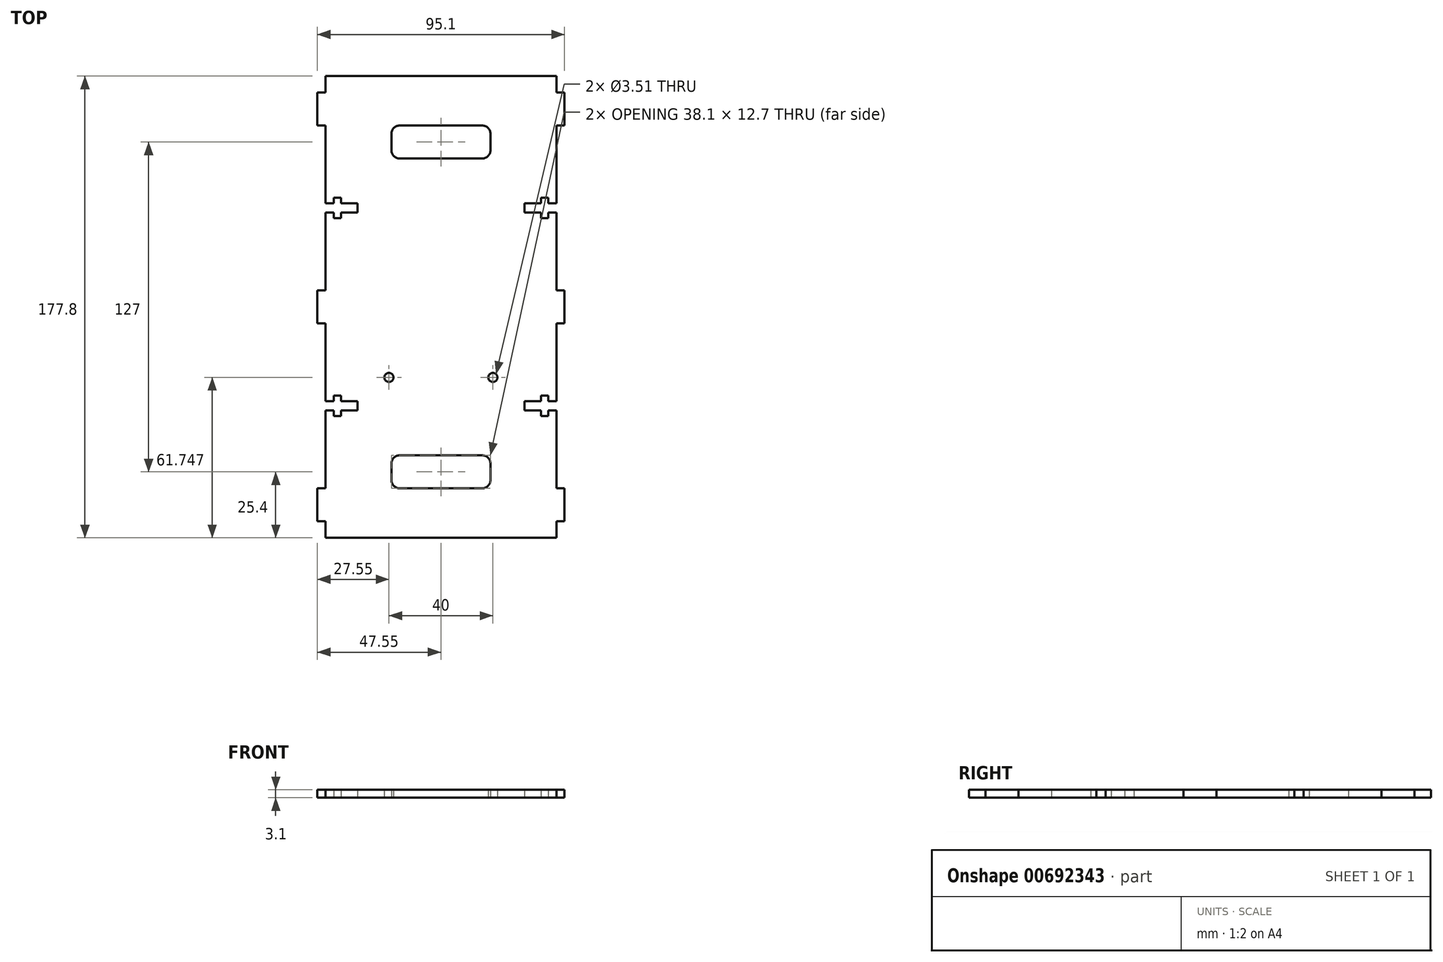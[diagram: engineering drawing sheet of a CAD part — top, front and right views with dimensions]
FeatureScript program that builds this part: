
annotation { "Feature Type Name" : "Feature", "Feature Type Description" : "" }
export const myFeature = defineFeature(function(context is Context, id is Id, definition is map)
    precondition{}
    {
        {
            var Q0;
            Q0=qCreatedBy(makeId("Top.planeOp"),FACE);
            var sketch = newSketch(context, id + "F0", { "sketchPlane" : qUnion([Q0])});
            skLineSegment(sketch, "E0.bottom", {"start": v(-44.45, 88.9) * mm, "end": v(44.45, 88.9) * mm});
            skLineSegment(sketch, "E0.top", {"start": v(-44.45, -88.9) * mm, "end": v(44.45, -88.9) * mm});
            skLineSegment(sketch, "E0.left", {"start": v(-44.45, 88.9) * mm, "end": v(-44.45, 82.55) * mm});
            skLineSegment(sketch, "E0.right", {"start": v(44.45, 88.9) * mm, "end": v(44.45, 82.55) * mm});
            skPoint(sketch, "E0.middle", {"position": v(0, 0) * mm});
            skCircle(sketch, "E1", {"center": v(-20, -27.15) * mm, "radius": 1.75 * mm});
            skCircle(sketch, "E2.MirrorC", {"center": v(20, -27.15) * mm, "radius": 1.75 * mm});
            skLineSegment(sketch, "E3", {"start": v(-44.45, 38.1) * mm, "end": v(44.45, 38.1) * mm, "construction": true});
            skLineSegment(sketch, "E4.bottom", {"start": v(-44.45, 39.85) * mm, "end": v(-41.27, 39.85) * mm});
            skLineSegment(sketch, "E4.top", {"start": v(-44.45, 36.35) * mm, "end": v(-41.27, 36.35) * mm});
            skPoint(sketch, "E4.middle", {"position": v(-42.86, 38.1) * mm});
            skLineSegment(sketch, "E5.bottom", {"start": v(-41.27, 42.07) * mm, "end": v(-38.5, 42.07) * mm});
            skLineSegment(sketch, "E5.top", {"start": v(-41.27, 34.13) * mm, "end": v(-38.5, 34.13) * mm});
            skLineSegment(sketch, "E5.left", {"start": v(-41.28, 42.07) * mm, "end": v(-41.28, 39.85) * mm});
            skLineSegment(sketch, "E5.right", {"start": v(-38.5, 42.07) * mm, "end": v(-38.5, 39.85) * mm});
            skPoint(sketch, "E5.middle", {"position": v(-39.89, 38.1) * mm});
            skLineSegment(sketch, "E6.bottom", {"start": v(-38.5, 39.85) * mm, "end": v(-32.15, 39.85) * mm});
            skLineSegment(sketch, "E6.top", {"start": v(-38.5, 36.35) * mm, "end": v(-32.15, 36.35) * mm});
            skLineSegment(sketch, "E6.right", {"start": v(-32.15, 39.85) * mm, "end": v(-32.15, 36.35) * mm});
            skPoint(sketch, "E6.middle", {"position": v(-35.32, 38.1) * mm});
            skLineSegment(sketch, "E7.trimOffspring", {"start": v(-41.28, 36.35) * mm, "end": v(-41.28, 34.13) * mm});
            skLineSegment(sketch, "E8.trimOffspring", {"start": v(-38.5, 36.35) * mm, "end": v(-38.5, 34.13) * mm});
            skLineSegment(sketch, "E9.trimOffspring", {"start": v(-44.45, 36.35) * mm, "end": v(-44.45, 6.35) * mm});
            skLineSegment(sketch, "E10.MirrorCS", {"start": v(-38.5, -36.35) * mm, "end": v(-38.5, -34.13) * mm});
            skLineSegment(sketch, "E11.MirrorCS", {"start": v(-38.5, -39.85) * mm, "end": v(-32.15, -39.85) * mm});
            skLineSegment(sketch, "E12.MirrorCS", {"start": v(-41.27, -36.35) * mm, "end": v(-41.27, -34.13) * mm});
            skLineSegment(sketch, "E13.MirrorCS", {"start": v(-38.5, -42.07) * mm, "end": v(-38.5, -39.85) * mm});
            skLineSegment(sketch, "E14.MirrorCS", {"start": v(-41.27, -42.07) * mm, "end": v(-41.27, -39.85) * mm});
            skLineSegment(sketch, "E15.MirrorCS", {"start": v(-41.27, -34.13) * mm, "end": v(-38.5, -34.13) * mm});
            skLineSegment(sketch, "E16.MirrorCS", {"start": v(-41.27, -42.07) * mm, "end": v(-38.5, -42.07) * mm});
            skLineSegment(sketch, "E17.MirrorCS", {"start": v(-44.45, -39.85) * mm, "end": v(-41.27, -39.85) * mm});
            skLineSegment(sketch, "E18.MirrorCS", {"start": v(-44.45, -36.35) * mm, "end": v(-41.27, -36.35) * mm});
            skPoint(sketch, "E19.MirrorP", {"position": v(-42.86, -38.1) * mm});
            skLineSegment(sketch, "E20.MirrorCS", {"start": v(-44.45, -36.35) * mm, "end": v(-44.45, -6.35) * mm});
            skPoint(sketch, "E21.MirrorP", {"position": v(-35.32, -38.1) * mm});
            skLineSegment(sketch, "E22.MirrorCS", {"start": v(-38.5, -36.35) * mm, "end": v(-32.15, -36.35) * mm});
            skLineSegment(sketch, "E23.MirrorCS", {"start": v(-32.15, -39.85) * mm, "end": v(-32.15, -36.35) * mm});
            skPoint(sketch, "E24.MirrorP", {"position": v(-39.89, -38.1) * mm});
            skLineSegment(sketch, "E25.MirrorCS", {"start": v(-44.45, -88.9) * mm, "end": v(-44.45, -82.55) * mm});
            skLineSegment(sketch, "E26.MirrorCS", {"start": v(-44.45, -38.1) * mm, "end": v(44.45, -38.1) * mm, "construction": true});
            skLineSegment(sketch, "E27.trimOffspring", {"start": v(-44.45, -39.85) * mm, "end": v(-44.45, -69.85) * mm});
            skLineSegment(sketch, "E28.trimOffspring", {"start": v(-44.45, 39.85) * mm, "end": v(-44.45, 69.85) * mm});
            skLineSegment(sketch, "E29.MirrorCS", {"start": v(44.45, 36.35) * mm, "end": v(41.27, 36.35) * mm});
            skLineSegment(sketch, "E30.MirrorCS", {"start": v(44.45, 39.85) * mm, "end": v(41.27, 39.85) * mm});
            skLineSegment(sketch, "E31.MirrorCS", {"start": v(38.5, 36.35) * mm, "end": v(38.5, 34.13) * mm});
            skPoint(sketch, "E32.MirrorP", {"position": v(42.86, 38.1) * mm});
            skLineSegment(sketch, "E33.MirrorCS", {"start": v(44.45, -39.85) * mm, "end": v(41.27, -39.85) * mm});
            skLineSegment(sketch, "E34.MirrorCS", {"start": v(44.45, -36.35) * mm, "end": v(41.27, -36.35) * mm});
            skLineSegment(sketch, "E35.MirrorCS", {"start": v(38.5, 42.07) * mm, "end": v(38.5, 39.85) * mm});
            skLineSegment(sketch, "E36.MirrorCS", {"start": v(41.27, 42.07) * mm, "end": v(41.27, 39.85) * mm});
            skLineSegment(sketch, "E37.MirrorCS", {"start": v(41.27, 34.13) * mm, "end": v(38.5, 34.13) * mm});
            skLineSegment(sketch, "E38.MirrorCS", {"start": v(41.27, 36.35) * mm, "end": v(41.27, 34.13) * mm});
            skLineSegment(sketch, "E39.MirrorCS", {"start": v(41.27, 42.07) * mm, "end": v(38.5, 42.07) * mm});
            skLineSegment(sketch, "E40.MirrorCS", {"start": v(38.5, -42.07) * mm, "end": v(38.5, -39.85) * mm});
            skLineSegment(sketch, "E41.MirrorCS", {"start": v(41.27, -42.07) * mm, "end": v(38.5, -42.07) * mm});
            skPoint(sketch, "E42.MirrorP", {"position": v(39.89, 38.1) * mm});
            skPoint(sketch, "E43.MirrorP", {"position": v(42.86, -38.1) * mm});
            skLineSegment(sketch, "E44.MirrorCS", {"start": v(32.15, -39.85) * mm, "end": v(32.15, -36.35) * mm});
            skLineSegment(sketch, "E45.MirrorCS", {"start": v(41.27, -36.35) * mm, "end": v(41.27, -34.13) * mm});
            skLineSegment(sketch, "E46.MirrorCS", {"start": v(41.27, -34.13) * mm, "end": v(38.5, -34.13) * mm});
            skLineSegment(sketch, "E47.MirrorCS", {"start": v(32.15, 39.85) * mm, "end": v(32.15, 36.35) * mm});
            skLineSegment(sketch, "E48.MirrorCS", {"start": v(41.27, -42.07) * mm, "end": v(41.27, -39.85) * mm});
            skPoint(sketch, "E49.MirrorP", {"position": v(39.89, -38.1) * mm});
            skLineSegment(sketch, "E50.MirrorCS", {"start": v(38.5, -36.35) * mm, "end": v(38.5, -34.13) * mm});
            skLineSegment(sketch, "E51.MirrorCS", {"start": v(44.45, -39.85) * mm, "end": v(44.45, -69.85) * mm});
            skLineSegment(sketch, "E52.MirrorCS", {"start": v(44.45, -36.35) * mm, "end": v(44.45, -6.35) * mm});
            skLineSegment(sketch, "E53.MirrorCS", {"start": v(38.5, 36.35) * mm, "end": v(32.15, 36.35) * mm});
            skLineSegment(sketch, "E54.MirrorCS", {"start": v(38.5, -36.35) * mm, "end": v(32.15, -36.35) * mm});
            skLineSegment(sketch, "E55.MirrorCS", {"start": v(38.5, -39.85) * mm, "end": v(32.15, -39.85) * mm});
            skLineSegment(sketch, "E56.MirrorCS", {"start": v(38.5, 39.85) * mm, "end": v(32.15, 39.85) * mm});
            skPoint(sketch, "E57.MirrorP", {"position": v(35.32, -38.1) * mm});
            skLineSegment(sketch, "E58.MirrorCS", {"start": v(44.45, 36.35) * mm, "end": v(44.45, 6.35) * mm});
            skLineSegment(sketch, "E59.MirrorCS", {"start": v(44.45, -38.1) * mm, "end": v(-44.45, -38.1) * mm, "construction": true});
            skPoint(sketch, "E60.MirrorP", {"position": v(35.32, 38.1) * mm});
            skLineSegment(sketch, "E61.MirrorCS", {"start": v(44.45, 39.85) * mm, "end": v(44.45, 69.85) * mm});
            skLineSegment(sketch, "E62.MirrorCS", {"start": v(44.45, 38.1) * mm, "end": v(-44.45, 38.1) * mm, "construction": true});
            skLineSegment(sketch, "E63.bottom", {"start": v(-19.05, -69.85) * mm, "end": v(19.05, -69.85) * mm});
            skLineSegment(sketch, "E63.top", {"start": v(-19.05, -57.15) * mm, "end": v(19.05, -57.15) * mm});
            skLineSegment(sketch, "E63.left", {"start": v(-19.05, -69.85) * mm, "end": v(-19.05, -57.15) * mm});
            skLineSegment(sketch, "E63.right", {"start": v(19.05, -69.85) * mm, "end": v(19.05, -57.15) * mm});
            skPoint(sketch, "E63.middle", {"position": v(0, -63.5) * mm});
            skPoint(sketch, "E64.MirrorP", {"position": v(0, 63.5) * mm});
            skLineSegment(sketch, "E65.MirrorCS", {"start": v(-19.05, 69.85) * mm, "end": v(19.05, 69.85) * mm});
            skLineSegment(sketch, "E66.MirrorCS", {"start": v(-19.05, 57.15) * mm, "end": v(19.05, 57.15) * mm});
            skLineSegment(sketch, "E67.MirrorCS", {"start": v(-19.05, 69.85) * mm, "end": v(-19.05, 57.15) * mm});
            skLineSegment(sketch, "E68.MirrorCS", {"start": v(19.05, 69.85) * mm, "end": v(19.05, 57.15) * mm});
            skLineSegment(sketch, "E69.bottom", {"start": v(-44.45, 6.35) * mm, "end": v(-47.55, 6.35) * mm});
            skLineSegment(sketch, "E69.top", {"start": v(-44.45, -6.35) * mm, "end": v(-47.55, -6.35) * mm});
            skLineSegment(sketch, "E69.right", {"start": v(-47.55, 6.35) * mm, "end": v(-47.55, -6.35) * mm});
            skPoint(sketch, "E69.middle", {"position": v(-46, 0) * mm});
            skLineSegment(sketch, "E70.bottom", {"start": v(-44.45, 82.55) * mm, "end": v(-47.55, 82.55) * mm});
            skLineSegment(sketch, "E70.top", {"start": v(-44.45, 69.85) * mm, "end": v(-47.55, 69.85) * mm});
            skLineSegment(sketch, "E70.right", {"start": v(-47.55, 82.55) * mm, "end": v(-47.55, 69.85) * mm});
            skPoint(sketch, "E70.middle", {"position": v(-46, 76.2) * mm});
            skLineSegment(sketch, "E71.trimOffspring", {"start": v(-44.45, -6.35) * mm, "end": v(-44.45, -36.35) * mm});
            skLineSegment(sketch, "E72.trimOffspring", {"start": v(-44.45, 6.35) * mm, "end": v(-44.45, 36.35) * mm});
            skLineSegment(sketch, "E73.trimOffspring", {"start": v(-44.45, 82.55) * mm, "end": v(-44.45, 88.9) * mm});
            skLineSegment(sketch, "E74.trimOffspring", {"start": v(-44.45, 69.85) * mm, "end": v(-44.45, 39.85) * mm});
            skLineSegment(sketch, "E75.MirrorCS", {"start": v(-44.45, -82.55) * mm, "end": v(-47.55, -82.55) * mm});
            skLineSegment(sketch, "E76.MirrorCS", {"start": v(-44.45, -69.85) * mm, "end": v(-47.55, -69.85) * mm});
            skLineSegment(sketch, "E77.MirrorCS", {"start": v(-47.55, -82.55) * mm, "end": v(-47.55, -69.85) * mm});
            skPoint(sketch, "E78.MirrorP", {"position": v(-46, -76.2) * mm});
            skLineSegment(sketch, "E79.trimOffspring", {"start": v(-44.45, -82.55) * mm, "end": v(-44.45, -88.9) * mm});
            skLineSegment(sketch, "E80.trimOffspring", {"start": v(-44.45, -69.85) * mm, "end": v(-44.45, -39.85) * mm});
            skLineSegment(sketch, "E81.MirrorCS", {"start": v(47.55, 82.55) * mm, "end": v(47.55, 69.85) * mm});
            skPoint(sketch, "E82.MirrorP", {"position": v(46, 76.2) * mm});
            skLineSegment(sketch, "E83.MirrorCS", {"start": v(44.45, 82.55) * mm, "end": v(47.55, 82.55) * mm});
            skLineSegment(sketch, "E84.MirrorCS", {"start": v(44.45, 69.85) * mm, "end": v(47.55, 69.85) * mm});
            skLineSegment(sketch, "E85.MirrorCS", {"start": v(44.45, -6.35) * mm, "end": v(47.55, -6.35) * mm});
            skLineSegment(sketch, "E86.MirrorCS", {"start": v(47.55, 6.35) * mm, "end": v(47.55, -6.35) * mm});
            skLineSegment(sketch, "E87.MirrorCS", {"start": v(44.45, 6.35) * mm, "end": v(47.55, 6.35) * mm});
            skPoint(sketch, "E88.MirrorP", {"position": v(46, 0) * mm});
            skLineSegment(sketch, "E89.MirrorCS", {"start": v(44.45, -82.55) * mm, "end": v(47.55, -82.55) * mm});
            skLineSegment(sketch, "E90.MirrorCS", {"start": v(44.45, -69.85) * mm, "end": v(47.55, -69.85) * mm});
            skLineSegment(sketch, "E91.MirrorCS", {"start": v(47.55, -82.55) * mm, "end": v(47.55, -69.85) * mm});
            skPoint(sketch, "E92.MirrorP", {"position": v(46, -76.2) * mm});
            skLineSegment(sketch, "E93.trimOffspring", {"start": v(44.45, -82.55) * mm, "end": v(44.45, -88.9) * mm});
            skLineSegment(sketch, "E94.trimOffspring", {"start": v(44.45, -6.35) * mm, "end": v(44.45, -36.35) * mm});
            skLineSegment(sketch, "E95.trimOffspring", {"start": v(44.45, 6.35) * mm, "end": v(44.45, 36.35) * mm});
            skLineSegment(sketch, "E96.trimOffspring", {"start": v(44.45, -69.85) * mm, "end": v(44.45, -39.85) * mm});
            skPoint(sketch, "E97.MirrorCS.start.orphan", {"position": v(44.45, -88.9) * mm});
            skLineSegment(sketch, "E98.trimOffspring", {"start": v(44.45, 69.85) * mm, "end": v(44.45, 39.85) * mm});
            skLineSegment(sketch, "E99.trimOffspring", {"start": v(44.45, 82.55) * mm, "end": v(44.45, 88.9) * mm});
            skSolve(sketch);
        }
        {
            var Q0;
            Q0=qSketchRegion(id+"F0",true);
            extrude(context, id + "F1", {"entities" : qUnion([Q0]), "depth" : 3.1 * mm, "offsetDistance" : 25.4 * mm});
        }
        {
            var Q0;
            Q0=makeQuery(id+"F1.opExtrude","SWEPT_EDGE",EDGE,{"disambiguationData":[OSD([sQuery(id+"F0.wireOp",EDGE,"E66.MirrorCS"),sQuery(id+"F0.wireOp",EDGE,"E68.MirrorCS")])]});
            var Q1;
            Q1=makeQuery(id+"F1.opExtrude","SWEPT_EDGE",EDGE,{"disambiguationData":[OSD([sQuery(id+"F0.wireOp",EDGE,"E63.bottom"),sQuery(id+"F0.wireOp",EDGE,"E63.right")])]});
            var Q2;
            Q2=makeQuery(id+"F1.opExtrude","SWEPT_EDGE",EDGE,{"disambiguationData":[OSD([sQuery(id+"F0.wireOp",EDGE,"E66.MirrorCS"),sQuery(id+"F0.wireOp",EDGE,"E67.MirrorCS")])]});
            var Q3;
            Q3=makeQuery(id+"F1.opExtrude","SWEPT_EDGE",EDGE,{"disambiguationData":[OSD([sQuery(id+"F0.wireOp",EDGE,"E63.bottom"),sQuery(id+"F0.wireOp",EDGE,"E63.left")])]});
            var Q4;
            Q4=makeQuery(id+"F1.opExtrude","SWEPT_EDGE",EDGE,{"disambiguationData":[OSD([sQuery(id+"F0.wireOp",EDGE,"E65.MirrorCS"),sQuery(id+"F0.wireOp",EDGE,"E68.MirrorCS")])]});
            var Q5;
            Q5=makeQuery(id+"F1.opExtrude","SWEPT_EDGE",EDGE,{"disambiguationData":[OSD([sQuery(id+"F0.wireOp",EDGE,"E63.top"),sQuery(id+"F0.wireOp",EDGE,"E63.right")])]});
            var Q6;
            Q6=makeQuery(id+"F1.opExtrude","SWEPT_EDGE",EDGE,{"disambiguationData":[OSD([sQuery(id+"F0.wireOp",EDGE,"E63.top"),sQuery(id+"F0.wireOp",EDGE,"E63.left")])]});
            var Q7;
            Q7=makeQuery(id+"F1.opExtrude","SWEPT_EDGE",EDGE,{"disambiguationData":[OSD([sQuery(id+"F0.wireOp",EDGE,"E65.MirrorCS"),sQuery(id+"F0.wireOp",EDGE,"E67.MirrorCS")])]});
            fillet(context, id + "F2", {"entities" : qUnion([Q0, Q1, Q2, Q3, Q4, Q5, Q6, Q7]), "radius" : 3.17 * mm, "tangentPropagation" : true, "allowEdgeOverflow" : false});
        }
    });
